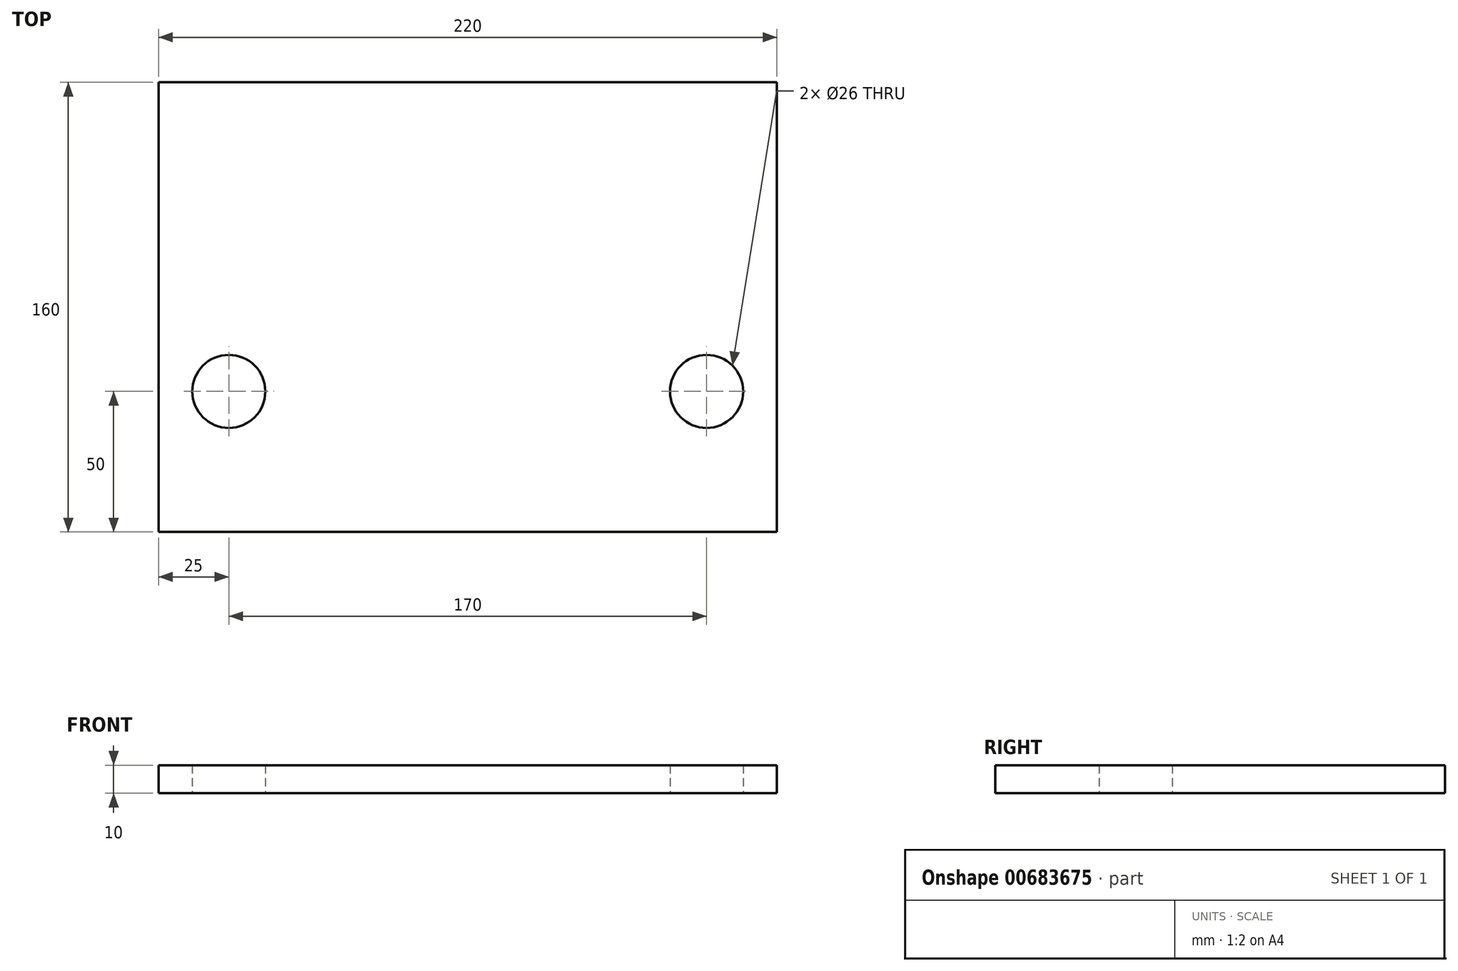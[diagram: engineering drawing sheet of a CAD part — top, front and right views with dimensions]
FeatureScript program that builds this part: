
annotation { "Feature Type Name" : "Feature", "Feature Type Description" : "" }
export const myFeature = defineFeature(function(context is Context, id is Id, definition is map)
    precondition{}
    {
        {
            var Q0;
            Q0=qCreatedBy(makeId("Top.planeOp"),FACE);
            var sketch = newSketch(context, id + "F0", { "sketchPlane" : qUnion([Q0])});
            skLineSegment(sketch, "E0.bottom", {"start": v(0, 0) * mm, "end": v(220, 0) * mm});
            skLineSegment(sketch, "E0.top", {"start": v(0, 160) * mm, "end": v(220, 160) * mm});
            skLineSegment(sketch, "E0.left", {"start": v(0, 0) * mm, "end": v(0, 160) * mm});
            skLineSegment(sketch, "E0.right", {"start": v(220, 0) * mm, "end": v(220, 160) * mm});
            skCircle(sketch, "E1", {"center": v(195, 50) * mm, "radius": 13 * mm});
            skCircle(sketch, "E2", {"center": v(25, 50) * mm, "radius": 13 * mm});
            skSolve(sketch);
        }
        {
            var Q0;
            Q0=makeQuery(id+"F0.imprint","IMPRINT",FACE,{"disambiguationData":[TD([[makeQuery(id+"F0.imprint","IMPRINT",EDGE,{"derivedFrom":sQuery(id+"F0.wireOp",EDGE,"E0.bottom")}),1.0]])]});
            extrude(context, id + "F1", {"entities" : qUnion([Q0]), "depth" : 10 * mm, "offsetDistance" : 25 * mm});
        }
    });
